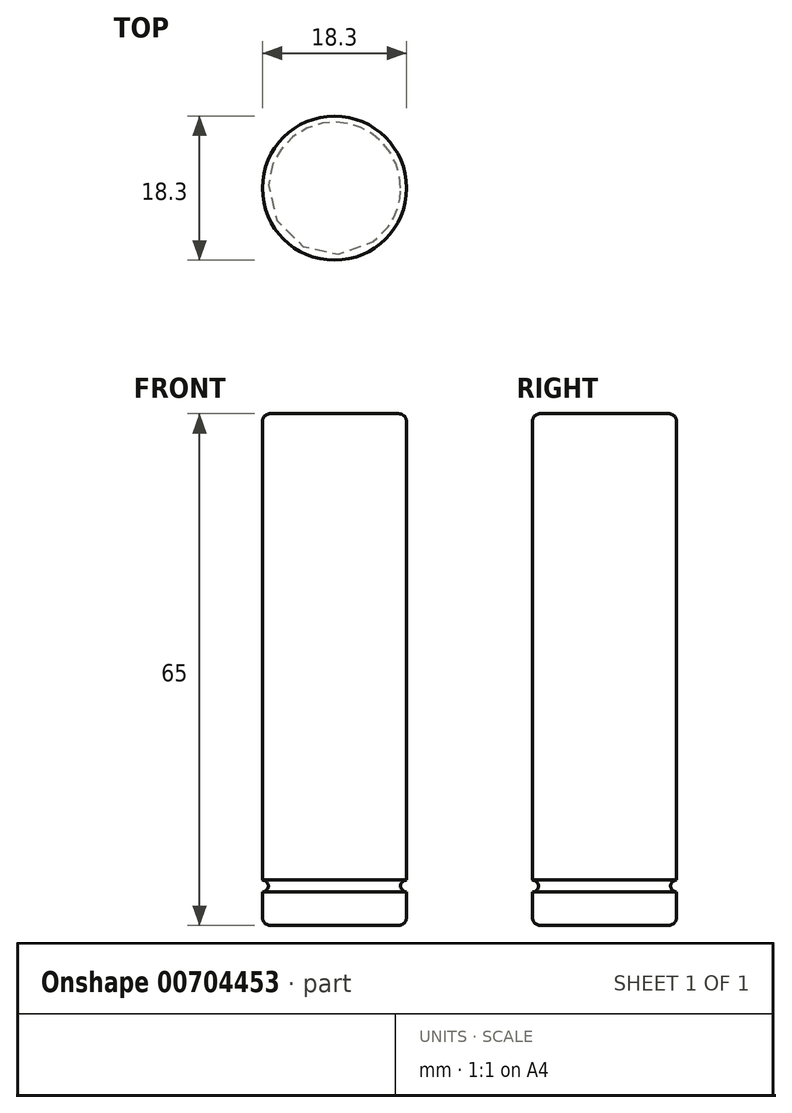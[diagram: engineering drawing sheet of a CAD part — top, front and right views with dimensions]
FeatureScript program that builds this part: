
annotation { "Feature Type Name" : "Feature", "Feature Type Description" : "" }
export const myFeature = defineFeature(function(context is Context, id is Id, definition is map)
    precondition{}
    {
        {
            var Q0;
            Q0=qCreatedBy(makeId("Top.planeOp"),FACE);
            var sketch = newSketch(context, id + "F0", { "sketchPlane" : qUnion([Q0])});
            skCircle(sketch, "E0", {"center": v(0, 0) * mm, "radius": 9.15 * mm});
            skSolve(sketch);
        }
        {
            var Q0;
            Q0=makeQuery(id+"F0.imprint","IMPRINT",FACE,{"disambiguationData":[TD([[makeQuery(id+"F0.imprint","IMPRINT",EDGE,{"derivedFrom":sQuery(id+"F0.wireOp",EDGE,"E0")}),1.0]])]});
            extrude(context, id + "F1", {"entities" : qUnion([Q0]), "depth" : 65 * mm, "offsetDistance" : 25 * mm});
        }
        {
            var Q0;
            Q0=qCreatedBy(makeId("Front.planeOp"),FACE);
            var sketch = newSketch(context, id + "F2", { "sketchPlane" : qUnion([Q0])});
            skLineSegment(sketch, "E1", {"start": v(9.15, 65) * mm, "end": v(9.15, 0) * mm});
            skLineSegment(sketch, "E2", {"start": v(0, 0) * mm, "end": v(0, 26.3) * mm, "construction": true});
            skArc(sketch, "E3", {"start": v(9.15, 5.75) * mm, "mid": v(8.4, 5) * mm, "end": v(9.15, 4.25) * mm});
            skSolve(sketch);
        }
        {
            var Q0;
            Q0 = qSketchRegion(id + "F2", true);
            var Q1;
            Q1=sQuery(id+"F2.wireOp",EDGE,"E2");
            revolve(context, id + "F3", {"operationType" : NewBodyOperationType.REMOVE, "surfaceOperationType" : NewSurfaceOperationType.NEW, "entities" : qUnion([Q0]), "axis" : qUnion([Q1]), "revolveType" : RevolveType.FULL, "oppositeDirection" : true});
        }
        {
            var Q0;
            Q0=makeQuery(id+"F1.opExtrude","CAP_EDGE",EDGE,{"disambiguationData":[OSD([sQuery(id+"F0.wireOp",EDGE,"E0")])],"isStart":false});
            var Q1;
            Q1=makeQuery(id+"F1.opExtrude","CAP_EDGE",EDGE,{"disambiguationData":[OSD([sQuery(id+"F0.wireOp",EDGE,"E0")])],"isStart":true});
            fillet(context, id + "F4", {"entities" : qUnion([Q0, Q1]), "tangentPropagation" : true, "radius" : 1 * mm, "defaultsChanged" : true, "vertexSettings" : [], "allowEdgeOverflow" : false});
        }
    });
